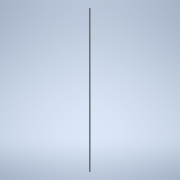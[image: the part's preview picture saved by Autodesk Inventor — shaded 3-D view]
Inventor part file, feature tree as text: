
AUTODESK INVENTOR PART (.ipt)
format: ipt  version: 2022 (Build 260153000, 153)  size: 148,992 bytes
history: native  units: mm
features: extrude x1, sketch x1
ambient origin geometry x8: Origin, YZ Plane, XZ Plane, XY Plane, X Axis, Y Axis, Z Axis, Center Point
bodies: Body1 (feature_tree)
feature tree (2):
  extrude  "Extrusion7"  Depth=5.0mm
  sketch  "Sketch4"  dims[d31=34.456mm d103=5.0mm d104=5.0mm d105=1952.0mm d106=0.0mm]
